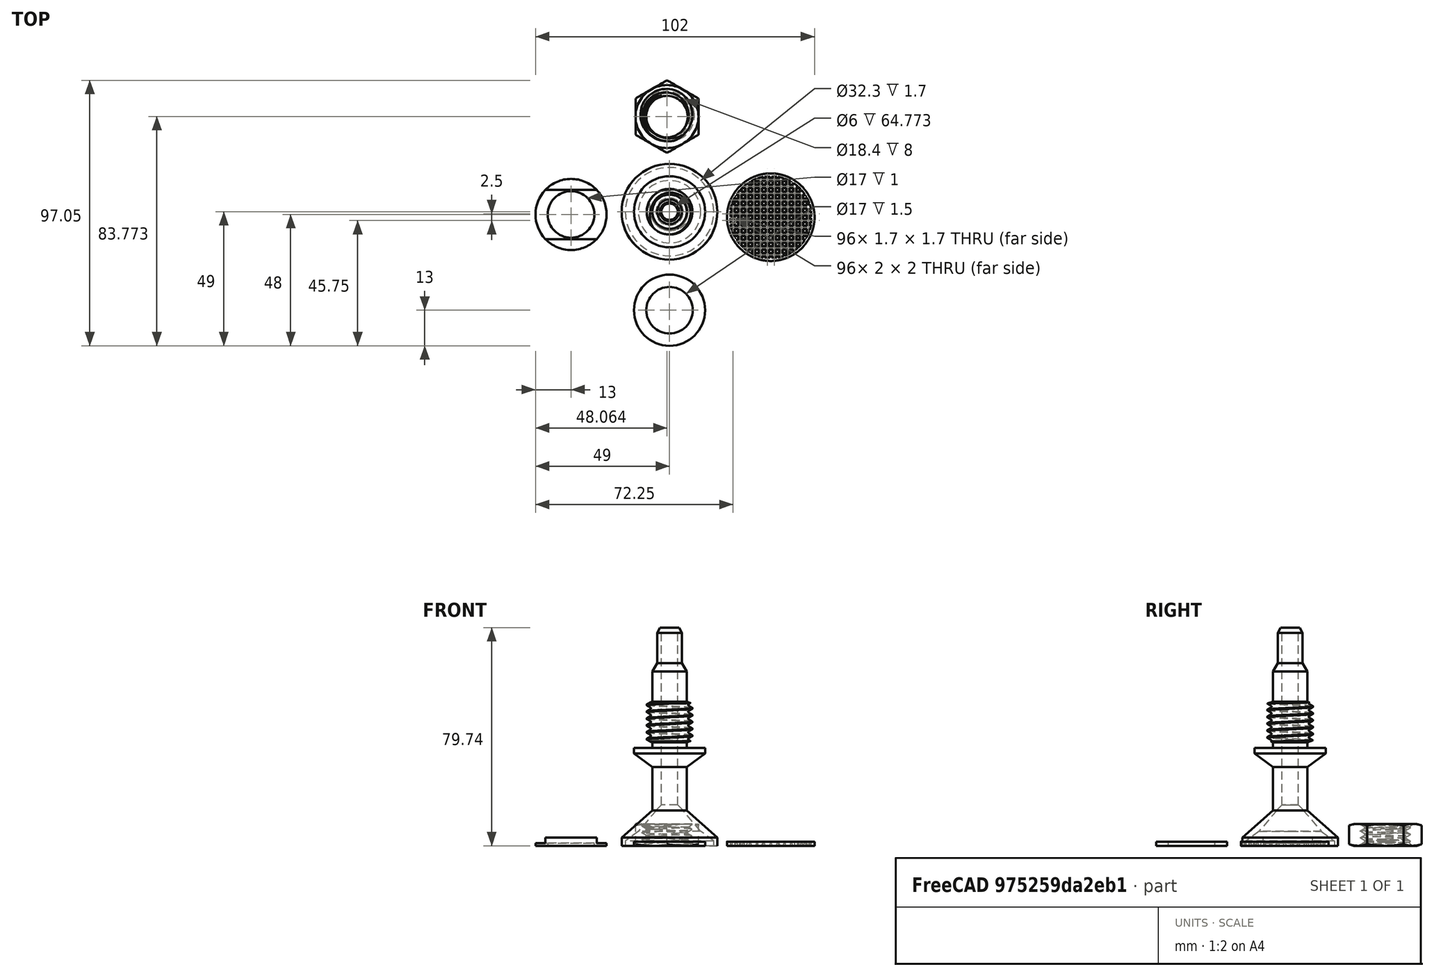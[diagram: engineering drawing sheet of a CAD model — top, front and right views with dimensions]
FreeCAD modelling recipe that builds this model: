
FCSTD DOCUMENT  (FreeCAD 0.18.4R)
Label: overflow.plug
License: All rights reserved
LicenseURL: http://en.wikipedia.org/wiki/All_rights_reserved
objects: Part::Cut×8, Part::Part2DObjectPython×8, Part::Extrusion×7, Part::Feature×6, Part::MultiFuse×3, Part::FeaturePython×2, App::DocumentObjectGroup×1
note: 34 computed .brp shape members not serialized (recipe doc carries the construction recipe); baked Part::Feature solids carry a one-line shape summary decoded from their .brp

FEATURE [Part::Cut] Cut001004011  label="Nut-R=9,003"
  Placement = pos=(-0.935979,34.7733,-37.7308) rot=(0,0,1;0rad)
FEATURE [Part::Feature] Fusion010013002001002004002003002003002  label="Fusion010013002001002004002003002005"
  shape: bbox 40.22 x 40.22 x 4.719 mm, 601 faces (baked)
FEATURE [Part::Feature] Fusion010013001  label="Pipe"
  shape: bbox 35 x 35 x 79.73 mm, 47 faces (baked)
FEATURE [Part::Feature] Fusion010013002001002004002001  label="Fusion010013002001002004003"
  shape: bbox 26 x 26 x 1.5 mm, 4 faces (baked)
FEATURE [Part::Feature] Fusion010013002001001  label="Fusion010013004"
  Placement = pos=(-33,53,0) rot=(0,0,1;0rad)
  shape: bbox 26 x 26 x 3 mm, 8 faces (baked)
FEATURE [Part::Part2DObjectPython] Circle  # Draft 2D object (typed FeaturePython)
  FirstAngle = 0
  LastAngle = 0
  MakeFace = true
  Placement = pos=(47.9585,46.9289,-33.2308) rot=(1,0,0;3.14159rad)
  Radius = 16
  Support = -> [Fusion010013001]
FEATURE [Part::Part2DObjectPython] Circle001  # Draft 2D object (typed FeaturePython)
  FirstAngle = 0
  LastAngle = 0
  MakeFace = true
  Placement = pos=(47.9585,46.9289,-33.2308) rot=(1,0,0;3.14159rad)
  Radius = 25.6251
  Support = -> [Circle]
FEATURE [Part::Extrusion] Extrusion
  Base = -> Circle
  Dir = (0,0,41.5)
  DirMode = 0
  FaceMakerClass = Part::FaceMakerBullseye
  LengthFwd = 0
  LengthRev = 0
  Solid = true
  Symmetric = false
FEATURE [Part::Extrusion] Extrusion001
  Base = -> Circle001
  Dir = (0,0,41.5)
  DirMode = 0
  FaceMakerClass = Part::FaceMakerBullseye
  LengthFwd = 0
  LengthRev = 0
  Solid = true
  Symmetric = false
FEATURE [Part::Cut] Cut
  Base = -> Extrusion001
  Placement = pos=(0,0,-20.75) rot=(0,0,1;0rad)
  Tool = -> Extrusion
FEATURE [Part::Part2DObjectPython] Circle002  # Draft 2D object (typed FeaturePython)
  FirstAngle = 0
  LastAngle = 0
  MakeFace = true
  Placement = pos=(47.9585,46.9289,-36.2308) rot=(0,0,1;0rad)
  Radius = 16
  Support = -> [Cut]
FEATURE [Part::Cut] Cut001004012
  Base = -> Fusion010013002001002004002003002003002
  Tool = -> Cut
FEATURE [Part::Part2DObjectPython] Circle003  # Draft 2D object (typed FeaturePython)
  FirstAngle = 0
  LastAngle = 0
  MakeFace = true
  Placement = pos=(47.9585,46.9289,-36.2308) rot=(0,0,1;0rad)
  Radius = 15
  Support = -> [Circle002]
FEATURE [Part::Extrusion] Extrusion002
  Base = -> Circle002
  Dir = (0,0,-1.5)
  DirMode = 0
  FaceMakerClass = Part::FaceMakerBullseye
  LengthFwd = 0
  LengthRev = 0
  Solid = true
  Symmetric = false
FEATURE [Part::Extrusion] Extrusion003
  Base = -> Circle003
  Dir = (0,0,-1.5)
  DirMode = 0
  FaceMakerClass = Part::FaceMakerBullseye
  LengthFwd = 0
  LengthRev = 0
  Solid = true
  Symmetric = false
FEATURE [Part::Cut] Cut001004013
  Base = -> Extrusion002
  Tool = -> Extrusion003
FEATURE [Part::Part2DObjectPython] Circle004  # Draft 2D object (typed FeaturePython)
  FirstAngle = 0
  LastAngle = 0
  MakeFace = true
  Placement = pos=(47.9585,46.9289,-36.2308) rot=(0,0,1;0rad)
  Radius = 16
  Support = -> [Cut001004012]
FEATURE [Part::Extrusion] Extrusion004
  Base = -> Circle004
  Dir = (0,0,-24.5)
  DirMode = 0
  FaceMakerClass = Part::FaceMakerBullseye
  LengthFwd = 0
  LengthRev = 0
  Solid = true
  Symmetric = false
FEATURE [Part::Part2DObjectPython] Circle005  # Draft 2D object (typed FeaturePython)
  FirstAngle = 0
  LastAngle = 0
  MakeFace = true
  Placement = pos=(47.9585,46.9289,-36.2308) rot=(0,0,1;0rad)
  Radius = 22.2117
  Support = -> [Extrusion004]
FEATURE [Part::Extrusion] Extrusion005
  Base = -> Circle005
  Dir = (0,0,-24.5)
  DirMode = 0
  FaceMakerClass = Part::FaceMakerBullseye
  LengthFwd = 0
  LengthRev = 0
  Solid = true
  Symmetric = false
FEATURE [Part::Cut] Cut001004014
  Base = -> Extrusion005
  Tool = -> Extrusion004
FEATURE [Part::MultiFuse] Fusion
  Shapes = -> [Cut001004012,Cut001004013]
FEATURE [Part::Cut] Cut001004015
  Base = -> Fusion
  Placement = pos=(-10.9585,-48.9289,6.39e-14) rot=(0,0,1;0rad)
  Tool = -> Cut001004014
FEATURE [Part::Part2DObjectPython] Circle006  # Draft 2D object (typed FeaturePython)
  FirstAngle = 0
  LastAngle = 0
  MakeFace = true
  Placement = pos=(0,0,-37.7308) rot=(1,0,0;3.14159rad)
  Radius = 16.15
  Support = -> [Cut001004015]
FEATURE [Part::Extrusion] Extrusion006
  Base = -> Circle006
  Dir = (0,0,1.7)
  DirMode = 0
  FaceMakerClass = Part::FaceMakerBullseye
  LengthFwd = 0
  LengthRev = 0
  Solid = true
  Symmetric = false
FEATURE [Part::Cut] Cut001004016
  Base = -> Fusion010013001
  Tool = -> Extrusion006
FEATURE [Part::Feature] Cut001004017
  shape: bbox 35 x 35 x 9.96 mm, 4 faces (baked)
FEATURE [Part::MultiFuse] Fusion010013002001002004002003002003003
  Shapes = -> [Cut001004017,Cut001004016]
FEATURE [Part::Feature] Cut001004015001  label="Cut001004018"
  shape: bbox 32.15 x 32.15 x 1.646 mm, 535 faces (baked)
FEATURE [Part::Part2DObjectPython] Rectangle  # Draft 2D object (typed FeaturePython)
  ChamferSize = 0
  Columns = 1
  FilletRadius = 0
  Height = 80.7618
  Length = 58.4439
  MakeFace = true
  Placement = pos=(-29.222,40.3809,-24.7731) rot=(1,0,0;3.14159rad)
  Rows = 1
FEATURE [Part::FeaturePython] Slice  # WARN: FeaturePython — macro-defined, semantics opaque (R4)
  Base = -> Fusion010013002001002004002003002003003
  Mode = 1
  Tolerance = 0
  Tools = -> [Rectangle]
FEATURE [Part::FeaturePython] Slice_child1  label="Slice.1"  # WARN: FeaturePython — macro-defined, semantics opaque (R4)
  Base = -> Slice
  FilterType = 1
  Invert = false
  OverrideMaxVal = 0
  WindowFrom = 80
  WindowTo = 100
  items = 1
FEATURE [Part::Cut] Cut001004018  label="Cut001004019"
  Base = -> Fusion
FEATURE [Part::MultiFuse] Fusion010013002001002004002003002003004
  Shapes = -> [Cut001004018,Slice_child1]
FEATURE [App::DocumentObjectGroup] GrExplode_Slice  label="Exploded Slice"
  Group = -> [Fusion010013002001002004002003002003004]
